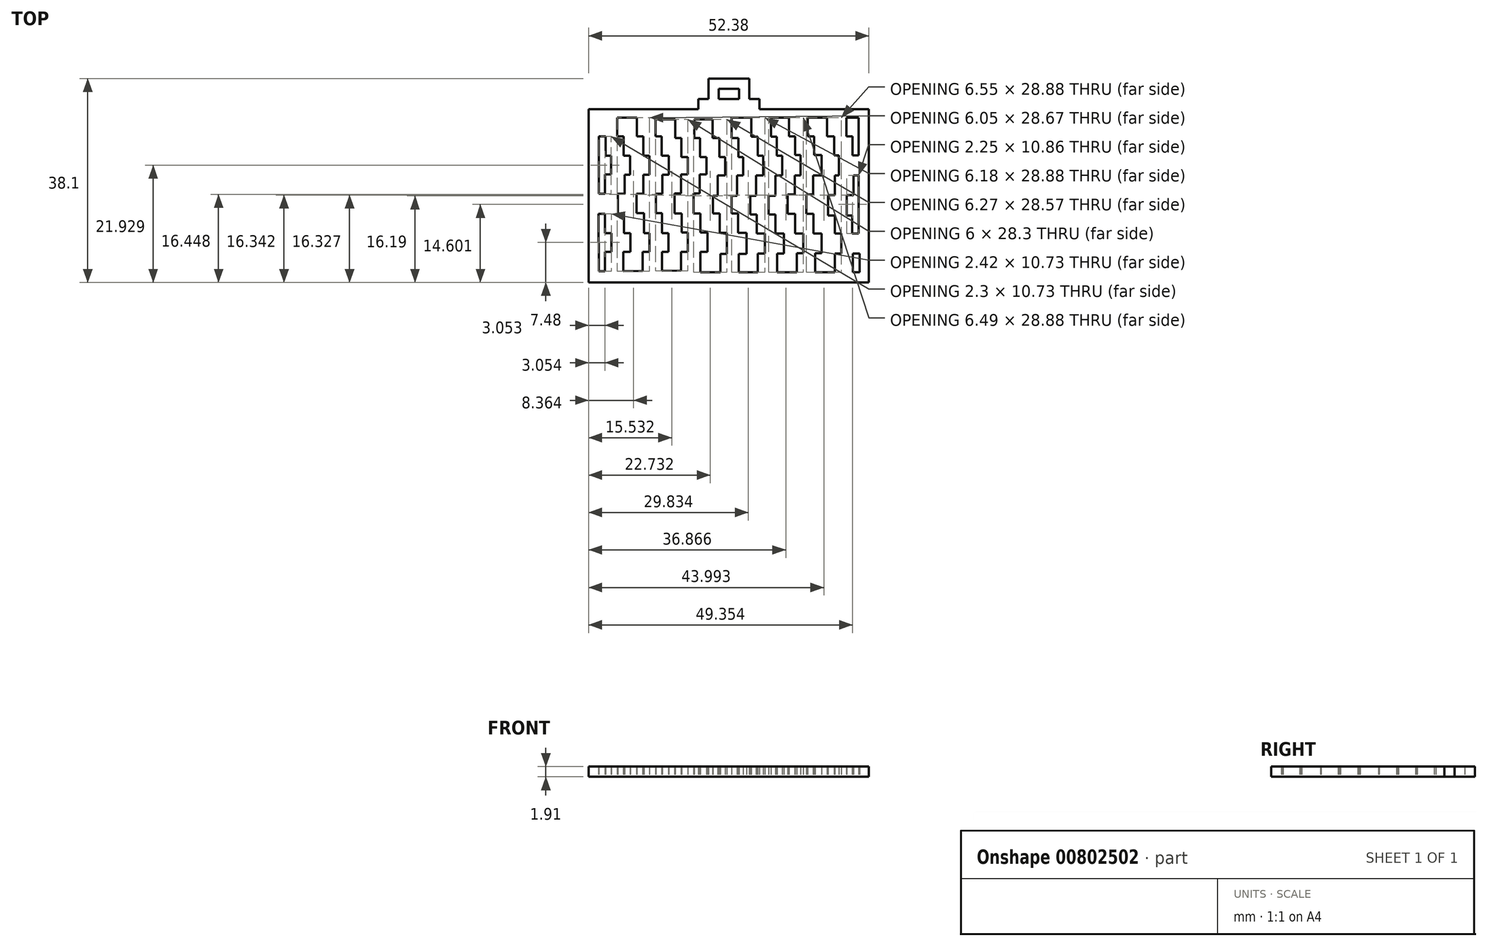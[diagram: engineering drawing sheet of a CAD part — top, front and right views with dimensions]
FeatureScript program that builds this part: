
annotation { "Feature Type Name" : "Feature", "Feature Type Description" : "" }
export const myFeature = defineFeature(function(context is Context, id is Id, definition is map)
    precondition{}
    {
        {
            var Q0;
            Q0=qCreatedBy(makeId("Top.planeOp"),FACE);
            var sketch = newSketch(context, id + "F0", { "sketchPlane" : qUnion([Q0])});
            skLineSegment(sketch, "E0.top", {"start": v(-16.2, 7.4) * mm, "end": v(-15.34, 7.4) * mm});
            skLineSegment(sketch, "E0.right", {"start": v(-13.9, 9.73) * mm, "end": v(-13.9, 7.4) * mm});
            skLineSegment(sketch, "E1.top", {"start": v(-15.34, 5) * mm, "end": v(-14.66, 5) * mm});
            skLineSegment(sketch, "E1.left", {"start": v(-15.34, 7.4) * mm, "end": v(-15.34, 5) * mm});
            skLineSegment(sketch, "E1.right", {"start": v(-13.1, 7.4) * mm, "end": v(-13.1, 5) * mm});
            skLineSegment(sketch, "E2.bottom", {"start": v(-13.1, 5) * mm, "end": v(-12.32, 5) * mm});
            skLineSegment(sketch, "E2.top", {"start": v(-12.99, 2.64) * mm, "end": v(-12.32, 2.64) * mm});
            skLineSegment(sketch, "E2.left", {"start": v(-14.66, 5) * mm, "end": v(-14.66, 2.64) * mm});
            skLineSegment(sketch, "E2.right", {"start": v(-12.32, 5) * mm, "end": v(-12.32, 2.64) * mm});
            skLineSegment(sketch, "E3.left", {"start": v(-11.46, 9.73) * mm, "end": v(-11.46, 7.4) * mm});
            skLineSegment(sketch, "E3.right", {"start": v(-9.1, 9.53) * mm, "end": v(-9.1, 7.4) * mm});
            skLineSegment(sketch, "E4.bottom", {"start": v(-9.1, 7.4) * mm, "end": v(-8.38, 7.4) * mm});
            skLineSegment(sketch, "E4.top", {"start": v(-10.65, 5.02) * mm, "end": v(-9.87, 5.02) * mm});
            skLineSegment(sketch, "E4.left", {"start": v(-10.65, 7.4) * mm, "end": v(-10.65, 5.02) * mm});
            skLineSegment(sketch, "E4.right", {"start": v(-8.38, 7.4) * mm, "end": v(-8.38, 5.02) * mm});
            skLineSegment(sketch, "E5.bottom", {"start": v(-8.38, 5.02) * mm, "end": v(-7.48, 5.02) * mm});
            skLineSegment(sketch, "E5.top", {"start": v(-8.3, 2.64) * mm, "end": v(-7.48, 2.64) * mm});
            skLineSegment(sketch, "E5.left", {"start": v(-9.87, 5.02) * mm, "end": v(-9.87, 2.64) * mm});
            skLineSegment(sketch, "E5.right", {"start": v(-7.48, 5.02) * mm, "end": v(-7.48, 2.64) * mm});
            skLineSegment(sketch, "E6.top", {"start": v(-6.66, 7.19) * mm, "end": v(-5.89, 7.19) * mm});
            skLineSegment(sketch, "E6.left", {"start": v(-6.66, 9.53) * mm, "end": v(-6.66, 7.19) * mm});
            skLineSegment(sketch, "E6.right", {"start": v(-4.3, 9.53) * mm, "end": v(-4.3, 7.19) * mm});
            skLineSegment(sketch, "E7.bottom", {"start": v(-4.3, 7.19) * mm, "end": v(-3.57, 7.19) * mm});
            skLineSegment(sketch, "E7.top", {"start": v(-5.89, 4.82) * mm, "end": v(-5.1, 4.82) * mm});
            skLineSegment(sketch, "E7.left", {"start": v(-5.89, 7.19) * mm, "end": v(-5.89, 4.82) * mm});
            skLineSegment(sketch, "E7.right", {"start": v(-3.57, 7.19) * mm, "end": v(-3.57, 4.82) * mm});
            skLineSegment(sketch, "E8.bottom", {"start": v(-3.57, 4.82) * mm, "end": v(-2.77, 4.82) * mm});
            skLineSegment(sketch, "E8.top", {"start": v(-3.63, 2.67) * mm, "end": v(-2.77, 2.67) * mm});
            skLineSegment(sketch, "E8.left", {"start": v(-5.1, 4.82) * mm, "end": v(-5.1, 2.67) * mm});
            skLineSegment(sketch, "E8.right", {"start": v(-2.77, 4.82) * mm, "end": v(-2.77, 2.67) * mm});
            skLineSegment(sketch, "E9.bottom", {"start": v(-15.44, 2.67) * mm, "end": v(-14.66, 2.67) * mm});
            skLineSegment(sketch, "E9.top", {"start": v(-13.84, 0.25) * mm, "end": v(-12.99, 0.25) * mm});
            skLineSegment(sketch, "E9.left", {"start": v(-15.44, 2.67) * mm, "end": v(-15.44, 0.25) * mm});
            skLineSegment(sketch, "E9.right", {"start": v(-12.99, 2.67) * mm, "end": v(-12.99, 0.25) * mm});
            skLineSegment(sketch, "E10.bottom", {"start": v(-15.44, 0.25) * mm, "end": v(-16.2, 0.25) * mm});
            skLineSegment(sketch, "E10.left", {"start": v(-13.84, 0.25) * mm, "end": v(-13.84, -2.23) * mm});
            skPoint(sketch, "E11.firstSnap0", {"position": v(-15.04, -2.23) * mm});
            skLineSegment(sketch, "E11.top", {"start": v(-15.44, -4.63) * mm, "end": v(-14.62, -4.63) * mm});
            skLineSegment(sketch, "E11.left", {"start": v(-15.44, -2.23) * mm, "end": v(-15.44, -4.63) * mm});
            skLineSegment(sketch, "E11.right", {"start": v(-13.04, -2.23) * mm, "end": v(-13.04, -4.63) * mm});
            skLineSegment(sketch, "E12.bottom", {"start": v(-13.04, -4.63) * mm, "end": v(-12.25, -4.63) * mm});
            skLineSegment(sketch, "E12.top", {"start": v(-13.13, -7) * mm, "end": v(-12.25, -7) * mm});
            skLineSegment(sketch, "E12.left", {"start": v(-14.62, -4.63) * mm, "end": v(-14.62, -7) * mm});
            skLineSegment(sketch, "E12.right", {"start": v(-12.25, -4.63) * mm, "end": v(-12.25, -7) * mm});
            skLineSegment(sketch, "E13.bottom", {"start": v(-14.62, -7) * mm, "end": v(-15.44, -7) * mm});
            skLineSegment(sketch, "E13.left", {"start": v(-13.13, -7) * mm, "end": v(-13.13, -9.38) * mm});
            skLineSegment(sketch, "E13.right", {"start": v(-15.44, -7) * mm, "end": v(-15.44, -9.38) * mm});
            skLineSegment(sketch, "E14.bottom", {"start": v(-9.87, 2.64) * mm, "end": v(-10.64, 2.64) * mm});
            skLineSegment(sketch, "E14.top", {"start": v(-8.3, 0.25) * mm, "end": v(-9.06, 0.25) * mm});
            skLineSegment(sketch, "E14.left", {"start": v(-8.3, 2.64) * mm, "end": v(-8.3, 0.25) * mm});
            skLineSegment(sketch, "E14.right", {"start": v(-10.64, 2.64) * mm, "end": v(-10.64, 0.25) * mm});
            skLineSegment(sketch, "E15.bottom", {"start": v(-10.64, 0.25) * mm, "end": v(-11.49, 0.25) * mm});
            skLineSegment(sketch, "E15.top", {"start": v(-10.56, -2.16) * mm, "end": v(-11.49, -2.16) * mm});
            skLineSegment(sketch, "E15.left", {"start": v(-9.06, 0.25) * mm, "end": v(-9.06, -2.16) * mm});
            skLineSegment(sketch, "E15.right", {"start": v(-11.49, 0.25) * mm, "end": v(-11.49, -2.16) * mm});
            skLineSegment(sketch, "E16.bottom", {"start": v(-9.06, -2.16) * mm, "end": v(-8.31, -2.16) * mm});
            skLineSegment(sketch, "E16.top", {"start": v(-10.56, -4.65) * mm, "end": v(-9.87, -4.65) * mm});
            skLineSegment(sketch, "E16.left", {"start": v(-10.56, -2.16) * mm, "end": v(-10.56, -4.65) * mm});
            skLineSegment(sketch, "E16.right", {"start": v(-8.31, -2.16) * mm, "end": v(-8.31, -4.65) * mm});
            skLineSegment(sketch, "E17.bottom", {"start": v(-8.31, -4.65) * mm, "end": v(-7.5, -4.65) * mm});
            skLineSegment(sketch, "E17.top", {"start": v(-8.31, -7) * mm, "end": v(-7.5, -7) * mm});
            skLineSegment(sketch, "E17.left", {"start": v(-9.87, -4.65) * mm, "end": v(-9.87, -7) * mm});
            skLineSegment(sketch, "E17.right", {"start": v(-7.5, -4.65) * mm, "end": v(-7.5, -7) * mm});
            skLineSegment(sketch, "E18.bottom", {"start": v(-10.74, -7) * mm, "end": v(-9.87, -7) * mm});
            skLineSegment(sketch, "E18.left", {"start": v(-10.74, -7) * mm, "end": v(-10.74, -9.34) * mm});
            skLineSegment(sketch, "E18.right", {"start": v(-8.31, -7) * mm, "end": v(-8.31, -9.34) * mm});
            skLineSegment(sketch, "E19.bottom", {"start": v(-5.1, 2.67) * mm, "end": v(-5.97, 2.67) * mm});
            skLineSegment(sketch, "E19.top", {"start": v(-3.63, 0.28) * mm, "end": v(-4.4, 0.28) * mm});
            skLineSegment(sketch, "E19.left", {"start": v(-3.63, 2.67) * mm, "end": v(-3.63, 0.28) * mm});
            skLineSegment(sketch, "E19.right", {"start": v(-5.97, 2.67) * mm, "end": v(-5.97, 0.28) * mm});
            skLineSegment(sketch, "E20.bottom", {"start": v(-5.97, 0.28) * mm, "end": v(-6.74, 0.28) * mm});
            skLineSegment(sketch, "E20.top", {"start": v(-5.86, -2.19) * mm, "end": v(-6.74, -2.19) * mm});
            skLineSegment(sketch, "E20.left", {"start": v(-4.4, 0.28) * mm, "end": v(-4.4, -2.19) * mm});
            skLineSegment(sketch, "E20.right", {"start": v(-6.74, 0.28) * mm, "end": v(-6.74, -2.19) * mm});
            skLineSegment(sketch, "E21.bottom", {"start": v(-4.4, -2.19) * mm, "end": v(-3.54, -2.19) * mm});
            skLineSegment(sketch, "E21.top", {"start": v(-5.86, -4.57) * mm, "end": v(-5.12, -4.57) * mm});
            skLineSegment(sketch, "E21.left", {"start": v(-5.86, -2.19) * mm, "end": v(-5.86, -4.57) * mm});
            skLineSegment(sketch, "E21.right", {"start": v(-3.54, -2.19) * mm, "end": v(-3.54, -4.57) * mm});
            skLineSegment(sketch, "E22.bottom", {"start": v(-3.54, -4.57) * mm, "end": v(-2.65, -4.57) * mm});
            skLineSegment(sketch, "E22.top", {"start": v(-3.55, -7) * mm, "end": v(-2.65, -7) * mm});
            skLineSegment(sketch, "E22.left", {"start": v(-5.12, -4.57) * mm, "end": v(-5.12, -7) * mm});
            skLineSegment(sketch, "E22.right", {"start": v(-2.65, -4.57) * mm, "end": v(-2.65, -7) * mm});
            skLineSegment(sketch, "E23.bottom", {"start": v(-5.12, -7) * mm, "end": v(-5.95, -7) * mm});
            skLineSegment(sketch, "E23.left", {"start": v(-3.55, -7) * mm, "end": v(-3.55, -9.52) * mm});
            skLineSegment(sketch, "E23.right", {"start": v(-5.95, -7) * mm, "end": v(-5.95, -9.32) * mm});
            skLineSegment(sketch, "E24.top", {"start": v(-2, 7.18) * mm, "end": v(-1.17, 7.18) * mm});
            skLineSegment(sketch, "E24.left", {"start": v(-2, 9.53) * mm, "end": v(-2, 7.18) * mm});
            skLineSegment(sketch, "E24.right", {"start": v(0.37, 9.73) * mm, "end": v(0.37, 7.18) * mm});
            skLineSegment(sketch, "E25.bottom", {"start": v(0.37, 7.18) * mm, "end": v(1.2, 7.18) * mm});
            skLineSegment(sketch, "E25.top", {"start": v(-1.17, 4.84) * mm, "end": v(-0.44, 4.84) * mm});
            skLineSegment(sketch, "E25.left", {"start": v(-1.17, 7.18) * mm, "end": v(-1.17, 4.84) * mm});
            skLineSegment(sketch, "E25.right", {"start": v(1.2, 7.18) * mm, "end": v(1.2, 4.84) * mm});
            skLineSegment(sketch, "E26.bottom", {"start": v(1.2, 4.84) * mm, "end": v(1.79, 4.84) * mm});
            skLineSegment(sketch, "E26.top", {"start": v(1.01, 2.56) * mm, "end": v(1.79, 2.56) * mm});
            skLineSegment(sketch, "E26.left", {"start": v(-0.44, 4.84) * mm, "end": v(-0.44, 2.56) * mm});
            skLineSegment(sketch, "E26.right", {"start": v(1.79, 4.84) * mm, "end": v(1.79, 2.56) * mm});
            skLineSegment(sketch, "E27.bottom", {"start": v(-0.44, 2.56) * mm, "end": v(-1.37, 2.56) * mm});
            skLineSegment(sketch, "E27.top", {"start": v(1.01, 0) * mm, "end": v(0.37, 0) * mm});
            skLineSegment(sketch, "E27.left", {"start": v(1.01, 2.56) * mm, "end": v(1.01, 0) * mm});
            skLineSegment(sketch, "E27.right", {"start": v(-1.37, 2.56) * mm, "end": v(-1.37, 0) * mm});
            skLineSegment(sketch, "E28.bottom", {"start": v(-1.37, 0) * mm, "end": v(-1.96, 0) * mm});
            skLineSegment(sketch, "E28.top", {"start": v(-1.1, -2.19) * mm, "end": v(-1.96, -2.19) * mm});
            skLineSegment(sketch, "E28.left", {"start": v(0.37, 0) * mm, "end": v(0.37, -2.19) * mm});
            skLineSegment(sketch, "E28.right", {"start": v(-1.96, 0) * mm, "end": v(-1.96, -2.19) * mm});
            skLineSegment(sketch, "E29.bottom", {"start": v(0.37, -2.19) * mm, "end": v(1.15, -2.19) * mm});
            skLineSegment(sketch, "E29.top", {"start": v(-1.1, -4.6) * mm, "end": v(-0.22, -4.6) * mm});
            skLineSegment(sketch, "E29.left", {"start": v(-1.1, -2.19) * mm, "end": v(-1.1, -4.6) * mm});
            skLineSegment(sketch, "E29.right", {"start": v(1.15, -2.19) * mm, "end": v(1.15, -4.6) * mm});
            skLineSegment(sketch, "E30.bottom", {"start": v(1.15, -4.6) * mm, "end": v(2.23, -4.6) * mm});
            skLineSegment(sketch, "E30.top", {"start": v(1.25, -7.25) * mm, "end": v(2.23, -7.25) * mm});
            skLineSegment(sketch, "E30.left", {"start": v(-0.22, -4.6) * mm, "end": v(-0.22, -7.25) * mm});
            skLineSegment(sketch, "E30.right", {"start": v(2.23, -4.6) * mm, "end": v(2.23, -7.25) * mm});
            skLineSegment(sketch, "E31.bottom", {"start": v(-0.22, -7.25) * mm, "end": v(-1.03, -7.25) * mm});
            skLineSegment(sketch, "E32.top", {"start": v(2.82, 7.38) * mm, "end": v(3.63, 7.38) * mm});
            skLineSegment(sketch, "E32.left", {"start": v(2.82, 9.73) * mm, "end": v(2.82, 7.38) * mm});
            skLineSegment(sketch, "E32.right", {"start": v(5.27, 9.73) * mm, "end": v(5.27, 7.38) * mm});
            skLineSegment(sketch, "E33.bottom", {"start": v(5.27, 7.38) * mm, "end": v(5.99, 7.38) * mm});
            skLineSegment(sketch, "E33.top", {"start": v(3.63, 5) * mm, "end": v(4.28, 5) * mm});
            skLineSegment(sketch, "E33.left", {"start": v(3.63, 7.38) * mm, "end": v(3.63, 5) * mm});
            skLineSegment(sketch, "E33.right", {"start": v(5.99, 7.38) * mm, "end": v(5.99, 5) * mm});
            skLineSegment(sketch, "E34.bottom", {"start": v(5.99, 5) * mm, "end": v(6.66, 5) * mm});
            skLineSegment(sketch, "E34.top", {"start": v(5.8, 2.56) * mm, "end": v(6.66, 2.56) * mm});
            skLineSegment(sketch, "E34.left", {"start": v(4.28, 5) * mm, "end": v(4.28, 2.56) * mm});
            skLineSegment(sketch, "E34.right", {"start": v(6.66, 5) * mm, "end": v(6.66, 2.56) * mm});
            skLineSegment(sketch, "E35.bottom", {"start": v(4.28, 2.56) * mm, "end": v(3.4, 2.56) * mm});
            skLineSegment(sketch, "E35.top", {"start": v(5.8, 0) * mm, "end": v(4.95, 0) * mm});
            skLineSegment(sketch, "E35.left", {"start": v(5.8, 2.56) * mm, "end": v(5.8, 0) * mm});
            skLineSegment(sketch, "E35.right", {"start": v(3.4, 2.56) * mm, "end": v(3.4, 0) * mm});
            skLineSegment(sketch, "E36.bottom", {"start": v(3.4, 0) * mm, "end": v(2.69, 0) * mm});
            skLineSegment(sketch, "E36.top", {"start": v(3.48, -2.33) * mm, "end": v(2.69, -2.33) * mm});
            skLineSegment(sketch, "E36.left", {"start": v(4.95, 0) * mm, "end": v(4.95, -2.33) * mm});
            skLineSegment(sketch, "E36.right", {"start": v(2.69, 0) * mm, "end": v(2.69, -2.33) * mm});
            skLineSegment(sketch, "E37.bottom", {"start": v(4.95, -2.33) * mm, "end": v(5.83, -2.33) * mm});
            skLineSegment(sketch, "E37.top", {"start": v(3.48, -4.68) * mm, "end": v(4.5, -4.68) * mm});
            skLineSegment(sketch, "E37.left", {"start": v(3.48, -2.33) * mm, "end": v(3.48, -4.68) * mm});
            skLineSegment(sketch, "E37.right", {"start": v(5.83, -2.33) * mm, "end": v(5.83, -4.68) * mm});
            skLineSegment(sketch, "E38.bottom", {"start": v(5.83, -4.68) * mm, "end": v(6.86, -4.68) * mm});
            skLineSegment(sketch, "E38.top", {"start": v(6.05, -7.17) * mm, "end": v(6.86, -7.17) * mm});
            skLineSegment(sketch, "E38.left", {"start": v(4.5, -4.68) * mm, "end": v(4.5, -7.17) * mm});
            skLineSegment(sketch, "E38.right", {"start": v(6.86, -4.68) * mm, "end": v(6.86, -7.17) * mm});
            skLineSegment(sketch, "E39.bottom", {"start": v(4.5, -7.17) * mm, "end": v(3.63, -7.17) * mm});
            skLineSegment(sketch, "E39.left", {"start": v(6.05, -7.17) * mm, "end": v(6.05, -9.52) * mm});
            skLineSegment(sketch, "E39.right", {"start": v(3.63, -7.17) * mm, "end": v(3.63, -9.52) * mm});
            skLineSegment(sketch, "E40.bottom", {"start": v(7.5, 9.73) * mm, "end": v(9.83, 9.73) * mm});
            skLineSegment(sketch, "E40.top", {"start": v(7.5, 7.4) * mm, "end": v(8.29, 7.4) * mm});
            skLineSegment(sketch, "E40.left", {"start": v(7.5, 9.73) * mm, "end": v(7.5, 7.4) * mm});
            skLineSegment(sketch, "E40.right", {"start": v(9.83, 9.73) * mm, "end": v(9.83, 7.4) * mm});
            skLineSegment(sketch, "E41.bottom", {"start": v(12.24, 9.73) * mm, "end": v(14.67, 9.73) * mm});
            skLineSegment(sketch, "E41.top", {"start": v(12.24, 7.4) * mm, "end": v(13.13, 7.4) * mm});
            skLineSegment(sketch, "E41.left", {"start": v(12.24, 9.73) * mm, "end": v(12.24, 7.4) * mm});
            skLineSegment(sketch, "E41.right", {"start": v(14.67, 9.73) * mm, "end": v(14.67, 7.4) * mm});
            skLineSegment(sketch, "E42.bottom", {"start": v(9.83, 7.4) * mm, "end": v(10.65, 7.4) * mm});
            skLineSegment(sketch, "E42.top", {"start": v(8.29, 5.07) * mm, "end": v(8.95, 5.07) * mm});
            skLineSegment(sketch, "E42.left", {"start": v(8.29, 7.4) * mm, "end": v(8.29, 5.07) * mm});
            skLineSegment(sketch, "E42.right", {"start": v(10.65, 7.4) * mm, "end": v(10.65, 5.07) * mm});
            skLineSegment(sketch, "E43.bottom", {"start": v(10.65, 5.07) * mm, "end": v(11.58, 5.07) * mm});
            skLineSegment(sketch, "E43.top", {"start": v(10.51, 2.56) * mm, "end": v(11.58, 2.56) * mm});
            skLineSegment(sketch, "E43.left", {"start": v(8.95, 5.07) * mm, "end": v(8.95, 2.56) * mm});
            skLineSegment(sketch, "E43.right", {"start": v(11.58, 5.07) * mm, "end": v(11.58, 2.56) * mm});
            skLineSegment(sketch, "E44.bottom", {"start": v(8.95, 2.56) * mm, "end": v(8.22, 2.56) * mm});
            skLineSegment(sketch, "E44.top", {"start": v(10.51, 0.18) * mm, "end": v(9.68, 0.18) * mm});
            skLineSegment(sketch, "E44.left", {"start": v(10.51, 2.56) * mm, "end": v(10.51, 0.18) * mm});
            skLineSegment(sketch, "E44.right", {"start": v(8.22, 2.56) * mm, "end": v(8.22, 0.18) * mm});
            skLineSegment(sketch, "E45.bottom", {"start": v(14.67, 7.4) * mm, "end": v(15.42, 7.4) * mm});
            skLineSegment(sketch, "E45.top", {"start": v(13.13, 5.03) * mm, "end": v(13.74, 5.03) * mm});
            skLineSegment(sketch, "E45.left", {"start": v(13.13, 7.4) * mm, "end": v(13.13, 5.03) * mm});
            skLineSegment(sketch, "E45.right", {"start": v(15.42, 7.4) * mm, "end": v(15.42, 5.03) * mm});
            skLineSegment(sketch, "E46.bottom", {"start": v(15.42, 5.03) * mm, "end": v(16.2, 5.03) * mm});
            skLineSegment(sketch, "E46.top", {"start": v(15.54, 2.56) * mm, "end": v(16.2, 2.56) * mm});
            skLineSegment(sketch, "E46.left", {"start": v(13.74, 5.03) * mm, "end": v(13.74, 2.56) * mm});
            skLineSegment(sketch, "E47.bottom", {"start": v(13.74, 2.56) * mm, "end": v(13.23, 2.56) * mm});
            skLineSegment(sketch, "E47.top", {"start": v(15.54, 0.1) * mm, "end": v(14.7, 0.1) * mm});
            skLineSegment(sketch, "E47.left", {"start": v(15.54, 2.56) * mm, "end": v(15.54, 0.1) * mm});
            skLineSegment(sketch, "E47.right", {"start": v(13.23, 2.56) * mm, "end": v(13.23, 0.1) * mm});
            skLineSegment(sketch, "E48.bottom", {"start": v(13.23, 0.1) * mm, "end": v(12.4, 0.1) * mm});
            skLineSegment(sketch, "E48.top", {"start": v(13.23, -2.47) * mm, "end": v(12.4, -2.47) * mm});
            skLineSegment(sketch, "E48.left", {"start": v(14.7, 0.1) * mm, "end": v(14.7, -2.47) * mm});
            skLineSegment(sketch, "E48.right", {"start": v(12.4, 0.1) * mm, "end": v(12.4, -2.47) * mm});
            skLineSegment(sketch, "E49.bottom", {"start": v(14.7, -2.47) * mm, "end": v(15.39, -2.47) * mm});
            skLineSegment(sketch, "E49.top", {"start": v(13.23, -4.68) * mm, "end": v(14.05, -4.68) * mm});
            skLineSegment(sketch, "E49.left", {"start": v(13.23, -2.47) * mm, "end": v(13.23, -4.68) * mm});
            skLineSegment(sketch, "E49.right", {"start": v(15.39, -2.47) * mm, "end": v(15.39, -4.68) * mm});
            skLineSegment(sketch, "E50.bottom", {"start": v(15.39, -4.68) * mm, "end": v(16.2, -4.68) * mm});
            skLineSegment(sketch, "E50.top", {"start": v(15.45, -7.2) * mm, "end": v(16.32, -7.2) * mm});
            skLineSegment(sketch, "E50.left", {"start": v(14.05, -4.68) * mm, "end": v(14.05, -7.2) * mm});
            skLineSegment(sketch, "E51.bottom", {"start": v(14.05, -7.2) * mm, "end": v(13.23, -7.2) * mm});
            skLineSegment(sketch, "E51.left", {"start": v(15.45, -7.2) * mm, "end": v(15.45, -9.52) * mm});
            skLineSegment(sketch, "E51.right", {"start": v(13.23, -7.2) * mm, "end": v(13.23, -9.52) * mm});
            skLineSegment(sketch, "E52.bottom", {"start": v(8.22, 0.18) * mm, "end": v(7.36, 0.18) * mm});
            skLineSegment(sketch, "E52.top", {"start": v(8.29, -2.24) * mm, "end": v(7.36, -2.24) * mm});
            skLineSegment(sketch, "E52.left", {"start": v(9.68, 0.18) * mm, "end": v(9.68, -2.24) * mm});
            skLineSegment(sketch, "E52.right", {"start": v(7.36, 0.18) * mm, "end": v(7.36, -2.24) * mm});
            skLineSegment(sketch, "E53.bottom", {"start": v(9.68, -2.24) * mm, "end": v(10.56, -2.24) * mm});
            skLineSegment(sketch, "E53.top", {"start": v(8.29, -4.68) * mm, "end": v(9.28, -4.68) * mm});
            skLineSegment(sketch, "E53.left", {"start": v(8.29, -2.24) * mm, "end": v(8.29, -4.68) * mm});
            skLineSegment(sketch, "E53.right", {"start": v(10.56, -2.24) * mm, "end": v(10.56, -4.68) * mm});
            skLineSegment(sketch, "E54.bottom", {"start": v(10.56, -4.68) * mm, "end": v(11.58, -4.68) * mm});
            skLineSegment(sketch, "E54.top", {"start": v(10.77, -7.15) * mm, "end": v(11.58, -7.15) * mm});
            skLineSegment(sketch, "E54.left", {"start": v(9.28, -4.68) * mm, "end": v(9.28, -7.15) * mm});
            skLineSegment(sketch, "E54.right", {"start": v(11.58, -4.68) * mm, "end": v(11.58, -7.15) * mm});
            skLineSegment(sketch, "E55.bottom", {"start": v(9.28, -7.15) * mm, "end": v(8.47, -7.15) * mm});
            skLineSegment(sketch, "E55.left", {"start": v(10.77, -7.15) * mm, "end": v(10.77, -9.52) * mm});
            skLineSegment(sketch, "E56", {"start": v(-13.9, 7.4) * mm, "end": v(-13.1, 7.4) * mm});
            skLineSegment(sketch, "E57.trimOffspring", {"start": v(-13.84, -2.23) * mm, "end": v(-13.04, -2.23) * mm});
            skLineSegment(sketch, "E58", {"start": v(-16.23, -2.23) * mm, "end": v(-15.44, -2.23) * mm});
            skLineSegment(sketch, "E59", {"start": v(-13.9, 9.73) * mm, "end": v(-11.46, 9.73) * mm});
            skLineSegment(sketch, "E60", {"start": v(-9.1, 9.53) * mm, "end": v(-6.66, 9.53) * mm});
            skLineSegment(sketch, "E61", {"start": v(-4.3, 9.53) * mm, "end": v(-2, 9.53) * mm});
            skLineSegment(sketch, "E62", {"start": v(2.82, 9.73) * mm, "end": v(0.37, 9.73) * mm});
            skLineSegment(sketch, "E63", {"start": v(5.27, 9.73) * mm, "end": v(7.5, 9.73) * mm});
            skLineSegment(sketch, "E64", {"start": v(9.83, 9.73) * mm, "end": v(12.24, 9.73) * mm});
            skPoint(sketch, "E65.firstSnap0", {"position": v(-0.88, 13.65) * mm});
            skLineSegment(sketch, "E66", {"start": v(-11.46, 7.4) * mm, "end": v(-10.65, 7.4) * mm});
            skPoint(sketch, "E67.end.orphan", {"position": v(14.56, 13.65) * mm});
            skPoint(sketch, "E68.end.orphan", {"position": v(-16.3, 13.65) * mm});
            skPoint(sketch, "E65.left.start.orphan", {"position": v(-0.88, 12.48) * mm});
            skLineSegment(sketch, "E69", {"start": v(-16.2, 7.4) * mm, "end": v(-16.2, 0.25) * mm});
            skLineSegment(sketch, "E70", {"start": v(-16.23, -2.23) * mm, "end": v(-16.2, -9.38) * mm});
            skLineSegment(sketch, "E71", {"start": v(-16.2, -9.38) * mm, "end": v(-15.44, -9.38) * mm});
            skLineSegment(sketch, "E72", {"start": v(-13.13, -9.38) * mm, "end": v(-10.74, -9.34) * mm});
            skLineSegment(sketch, "E73", {"start": v(-8.31, -9.34) * mm, "end": v(-5.95, -9.32) * mm});
            skLineSegment(sketch, "E74", {"start": v(-1.03, -7.25) * mm, "end": v(-1.03, -9.52) * mm});
            skLineSegment(sketch, "E75", {"start": v(-1.03, -9.52) * mm, "end": v(-3.55, -9.52) * mm});
            skLineSegment(sketch, "E76", {"start": v(1.25, -9.52) * mm, "end": v(3.63, -9.52) * mm});
            skLineSegment(sketch, "E77", {"start": v(1.25, -7.25) * mm, "end": v(1.25, -9.52) * mm});
            skLineSegment(sketch, "E78", {"start": v(12.54, -9.52) * mm, "end": v(13.23, -9.52) * mm});
            skLineSegment(sketch, "E79", {"start": v(16.2, 5.03) * mm, "end": v(16.2, 9.73) * mm});
            skLineSegment(sketch, "E80", {"start": v(14.67, 9.73) * mm, "end": v(16.2, 9.73) * mm});
            skLineSegment(sketch, "E81", {"start": v(8.47, -7.15) * mm, "end": v(8.47, -9.52) * mm});
            skLineSegment(sketch, "E82.bottom", {"start": v(-17.46, 10.8) * mm, "end": v(-3.81, 10.8) * mm});
            skLineSegment(sketch, "E82.top", {"start": v(-17.46, -10.8) * mm, "end": v(17.46, -10.8) * mm});
            skLineSegment(sketch, "E82.left", {"start": v(-17.46, 10.8) * mm, "end": v(-17.46, -10.8) * mm});
            skLineSegment(sketch, "E82.right", {"start": v(17.46, 10.8) * mm, "end": v(17.46, -10.8) * mm});
            skLineSegment(sketch, "E83.trimOffspring", {"start": v(6.05, -9.52) * mm, "end": v(8.47, -9.52) * mm});
            skLineSegment(sketch, "E84.trimOffspring", {"start": v(10.77, -9.52) * mm, "end": v(12.54, -9.52) * mm});
            skLineSegment(sketch, "E85.trimOffspring", {"start": v(15.45, -9.52) * mm, "end": v(16.32, -9.52) * mm});
            skLineSegment(sketch, "E86.trimOffspring", {"start": v(16.32, -7.2) * mm, "end": v(16.32, -9.52) * mm});
            skLineSegment(sketch, "E87", {"start": v(16.2, 2.56) * mm, "end": v(16.2, -4.68) * mm});
            skLineSegment(sketch, "E88.bottom", {"start": v(1.27, 13.34) * mm, "end": v(-1.27, 13.34) * mm});
            skLineSegment(sketch, "E88.top", {"start": v(1.27, 12.07) * mm, "end": v(-1.27, 12.07) * mm});
            skLineSegment(sketch, "E88.left", {"start": v(1.27, 13.34) * mm, "end": v(1.27, 12.07) * mm});
            skLineSegment(sketch, "E88.right", {"start": v(-1.27, 13.34) * mm, "end": v(-1.27, 12.07) * mm});
            skLineSegment(sketch, "E89", {"start": v(-3.81, 10.8) * mm, "end": v(-3.81, 12.07) * mm});
            skLineSegment(sketch, "E90", {"start": v(-3.81, 12.07) * mm, "end": v(-2.54, 12.07) * mm});
            skLineSegment(sketch, "E91", {"start": v(-2.54, 12.07) * mm, "end": v(-2.54, 14.6) * mm});
            skLineSegment(sketch, "E92", {"start": v(-2.54, 14.6) * mm, "end": v(2.54, 14.6) * mm});
            skLineSegment(sketch, "E93", {"start": v(2.54, 14.6) * mm, "end": v(2.54, 12.07) * mm});
            skLineSegment(sketch, "E94", {"start": v(2.54, 12.07) * mm, "end": v(3.81, 12.07) * mm});
            skLineSegment(sketch, "E95", {"start": v(3.81, 12.07) * mm, "end": v(3.81, 10.8) * mm});
            skLineSegment(sketch, "E96.trimOffspring", {"start": v(3.81, 10.8) * mm, "end": v(17.46, 10.8) * mm});
            skSolve(sketch);
        }
        {
            var Q0;
            Q0 = qSketchRegion(id + "F0", true);
            extrude(context, id + "F1", {"entities" : qUnion([Q0]), "depth" : 1.27 * mm, "offsetDistance" : 25.4 * mm});
        }
        {
            var Q0;
            Q0=makeQuery(id+"F1.opExtrude","SWEPT_BODY",BODY,{"disambiguationData":[OSD([sQuery(id+"F0.wireOp",EDGE,"E0.top"),sQuery(id+"F0.wireOp",EDGE,"E0.right"),sQuery(id+"F0.wireOp",EDGE,"E1.top"),sQuery(id+"F0.wireOp",EDGE,"E1.left"),sQuery(id+"F0.wireOp",EDGE,"E1.right"),sQuery(id+"F0.wireOp",EDGE,"E2.bottom"),sQuery(id+"F0.wireOp",EDGE,"E2.top"),sQuery(id+"F0.wireOp",EDGE,"E2.left"),sQuery(id+"F0.wireOp",EDGE,"E2.right"),sQuery(id+"F0.wireOp",EDGE,"E3.left"),sQuery(id+"F0.wireOp",EDGE,"E3.right"),sQuery(id+"F0.wireOp",EDGE,"E4.bottom"),sQuery(id+"F0.wireOp",EDGE,"E4.top"),sQuery(id+"F0.wireOp",EDGE,"E4.left"),sQuery(id+"F0.wireOp",EDGE,"E4.right"),sQuery(id+"F0.wireOp",EDGE,"E5.bottom"),sQuery(id+"F0.wireOp",EDGE,"E5.top"),sQuery(id+"F0.wireOp",EDGE,"E5.left"),sQuery(id+"F0.wireOp",EDGE,"E5.right"),sQuery(id+"F0.wireOp",EDGE,"E6.top"),sQuery(id+"F0.wireOp",EDGE,"E6.left"),sQuery(id+"F0.wireOp",EDGE,"E6.right"),sQuery(id+"F0.wireOp",EDGE,"E7.bottom"),sQuery(id+"F0.wireOp",EDGE,"E7.top"),sQuery(id+"F0.wireOp",EDGE,"E7.left"),sQuery(id+"F0.wireOp",EDGE,"E7.right"),sQuery(id+"F0.wireOp",EDGE,"E8.bottom"),sQuery(id+"F0.wireOp",EDGE,"E8.top"),sQuery(id+"F0.wireOp",EDGE,"E8.left"),sQuery(id+"F0.wireOp",EDGE,"E8.right"),sQuery(id+"F0.wireOp",EDGE,"E9.bottom"),sQuery(id+"F0.wireOp",EDGE,"E9.top"),sQuery(id+"F0.wireOp",EDGE,"E9.left"),sQuery(id+"F0.wireOp",EDGE,"E9.right"),sQuery(id+"F0.wireOp",EDGE,"E10.bottom"),sQuery(id+"F0.wireOp",EDGE,"E10.left"),sQuery(id+"F0.wireOp",EDGE,"E11.top"),sQuery(id+"F0.wireOp",EDGE,"E11.left"),sQuery(id+"F0.wireOp",EDGE,"E11.right"),sQuery(id+"F0.wireOp",EDGE,"E12.bottom"),sQuery(id+"F0.wireOp",EDGE,"E12.top"),sQuery(id+"F0.wireOp",EDGE,"E12.left"),sQuery(id+"F0.wireOp",EDGE,"E12.right"),sQuery(id+"F0.wireOp",EDGE,"E13.bottom"),sQuery(id+"F0.wireOp",EDGE,"E13.left"),sQuery(id+"F0.wireOp",EDGE,"E13.right"),sQuery(id+"F0.wireOp",EDGE,"E14.bottom"),sQuery(id+"F0.wireOp",EDGE,"E14.top"),sQuery(id+"F0.wireOp",EDGE,"E14.left"),sQuery(id+"F0.wireOp",EDGE,"E14.right"),sQuery(id+"F0.wireOp",EDGE,"E15.bottom"),sQuery(id+"F0.wireOp",EDGE,"E15.top"),sQuery(id+"F0.wireOp",EDGE,"E15.left"),sQuery(id+"F0.wireOp",EDGE,"E15.right"),sQuery(id+"F0.wireOp",EDGE,"E16.bottom"),sQuery(id+"F0.wireOp",EDGE,"E16.top"),sQuery(id+"F0.wireOp",EDGE,"E16.left"),sQuery(id+"F0.wireOp",EDGE,"E16.right"),sQuery(id+"F0.wireOp",EDGE,"E17.bottom"),sQuery(id+"F0.wireOp",EDGE,"E17.top"),sQuery(id+"F0.wireOp",EDGE,"E17.left"),sQuery(id+"F0.wireOp",EDGE,"E17.right"),sQuery(id+"F0.wireOp",EDGE,"E18.bottom"),sQuery(id+"F0.wireOp",EDGE,"E18.left"),sQuery(id+"F0.wireOp",EDGE,"E18.right"),sQuery(id+"F0.wireOp",EDGE,"E19.bottom"),sQuery(id+"F0.wireOp",EDGE,"E19.top"),sQuery(id+"F0.wireOp",EDGE,"E19.left"),sQuery(id+"F0.wireOp",EDGE,"E19.right"),sQuery(id+"F0.wireOp",EDGE,"E20.bottom"),sQuery(id+"F0.wireOp",EDGE,"E20.top"),sQuery(id+"F0.wireOp",EDGE,"E20.left"),sQuery(id+"F0.wireOp",EDGE,"E20.right"),sQuery(id+"F0.wireOp",EDGE,"E21.bottom"),sQuery(id+"F0.wireOp",EDGE,"E21.top"),sQuery(id+"F0.wireOp",EDGE,"E21.left"),sQuery(id+"F0.wireOp",EDGE,"E21.right"),sQuery(id+"F0.wireOp",EDGE,"E22.bottom"),sQuery(id+"F0.wireOp",EDGE,"E22.top"),sQuery(id+"F0.wireOp",EDGE,"E22.left"),sQuery(id+"F0.wireOp",EDGE,"E22.right"),sQuery(id+"F0.wireOp",EDGE,"E23.bottom"),sQuery(id+"F0.wireOp",EDGE,"E23.left"),sQuery(id+"F0.wireOp",EDGE,"E23.right"),sQuery(id+"F0.wireOp",EDGE,"E24.top"),sQuery(id+"F0.wireOp",EDGE,"E24.left"),sQuery(id+"F0.wireOp",EDGE,"E24.right"),sQuery(id+"F0.wireOp",EDGE,"E25.bottom"),sQuery(id+"F0.wireOp",EDGE,"E25.top"),sQuery(id+"F0.wireOp",EDGE,"E25.left"),sQuery(id+"F0.wireOp",EDGE,"E25.right"),sQuery(id+"F0.wireOp",EDGE,"E26.bottom"),sQuery(id+"F0.wireOp",EDGE,"E26.top"),sQuery(id+"F0.wireOp",EDGE,"E26.left"),sQuery(id+"F0.wireOp",EDGE,"E26.right"),sQuery(id+"F0.wireOp",EDGE,"E27.bottom"),sQuery(id+"F0.wireOp",EDGE,"E27.top"),sQuery(id+"F0.wireOp",EDGE,"E27.left"),sQuery(id+"F0.wireOp",EDGE,"E27.right"),sQuery(id+"F0.wireOp",EDGE,"E28.top"),sQuery(id+"F0.wireOp",EDGE,"E28.left"),sQuery(id+"F0.wireOp",EDGE,"E28.right"),sQuery(id+"F0.wireOp",EDGE,"E29.bottom"),sQuery(id+"F0.wireOp",EDGE,"E29.top"),sQuery(id+"F0.wireOp",EDGE,"E29.left"),sQuery(id+"F0.wireOp",EDGE,"E29.right"),sQuery(id+"F0.wireOp",EDGE,"E30.bottom"),sQuery(id+"F0.wireOp",EDGE,"E30.top"),sQuery(id+"F0.wireOp",EDGE,"E30.left"),sQuery(id+"F0.wireOp",EDGE,"E30.right"),sQuery(id+"F0.wireOp",EDGE,"E31.bottom"),sQuery(id+"F0.wireOp",EDGE,"E32.top"),sQuery(id+"F0.wireOp",EDGE,"E32.left"),sQuery(id+"F0.wireOp",EDGE,"E32.right"),sQuery(id+"F0.wireOp",EDGE,"E33.bottom"),sQuery(id+"F0.wireOp",EDGE,"E33.top"),sQuery(id+"F0.wireOp",EDGE,"E33.left"),sQuery(id+"F0.wireOp",EDGE,"E33.right"),sQuery(id+"F0.wireOp",EDGE,"E34.bottom"),sQuery(id+"F0.wireOp",EDGE,"E34.top"),sQuery(id+"F0.wireOp",EDGE,"E34.left"),sQuery(id+"F0.wireOp",EDGE,"E34.right"),sQuery(id+"F0.wireOp",EDGE,"E35.bottom"),sQuery(id+"F0.wireOp",EDGE,"E35.top"),sQuery(id+"F0.wireOp",EDGE,"E35.left"),sQuery(id+"F0.wireOp",EDGE,"E35.right"),sQuery(id+"F0.wireOp",EDGE,"E36.bottom"),sQuery(id+"F0.wireOp",EDGE,"E36.top"),sQuery(id+"F0.wireOp",EDGE,"E36.left"),sQuery(id+"F0.wireOp",EDGE,"E36.right"),sQuery(id+"F0.wireOp",EDGE,"E37.bottom"),sQuery(id+"F0.wireOp",EDGE,"E37.top"),sQuery(id+"F0.wireOp",EDGE,"E37.left"),sQuery(id+"F0.wireOp",EDGE,"E37.right"),sQuery(id+"F0.wireOp",EDGE,"E38.bottom"),sQuery(id+"F0.wireOp",EDGE,"E38.top"),sQuery(id+"F0.wireOp",EDGE,"E38.left"),sQuery(id+"F0.wireOp",EDGE,"E38.right"),sQuery(id+"F0.wireOp",EDGE,"E39.bottom"),sQuery(id+"F0.wireOp",EDGE,"E39.left"),sQuery(id+"F0.wireOp",EDGE,"E39.right"),sQuery(id+"F0.wireOp",EDGE,"E40.top"),sQuery(id+"F0.wireOp",EDGE,"E40.left"),sQuery(id+"F0.wireOp",EDGE,"E40.right"),sQuery(id+"F0.wireOp",EDGE,"E41.top"),sQuery(id+"F0.wireOp",EDGE,"E41.left"),sQuery(id+"F0.wireOp",EDGE,"E41.right"),sQuery(id+"F0.wireOp",EDGE,"E42.bottom"),sQuery(id+"F0.wireOp",EDGE,"E42.top"),sQuery(id+"F0.wireOp",EDGE,"E42.left"),sQuery(id+"F0.wireOp",EDGE,"E42.right"),sQuery(id+"F0.wireOp",EDGE,"E43.bottom"),sQuery(id+"F0.wireOp",EDGE,"E43.top"),sQuery(id+"F0.wireOp",EDGE,"E43.left"),sQuery(id+"F0.wireOp",EDGE,"E43.right"),sQuery(id+"F0.wireOp",EDGE,"E44.bottom"),sQuery(id+"F0.wireOp",EDGE,"E44.top"),sQuery(id+"F0.wireOp",EDGE,"E44.left"),sQuery(id+"F0.wireOp",EDGE,"E44.right"),sQuery(id+"F0.wireOp",EDGE,"E45.bottom"),sQuery(id+"F0.wireOp",EDGE,"E45.top"),sQuery(id+"F0.wireOp",EDGE,"E45.left"),sQuery(id+"F0.wireOp",EDGE,"E45.right"),sQuery(id+"F0.wireOp",EDGE,"E46.bottom"),sQuery(id+"F0.wireOp",EDGE,"E46.top"),sQuery(id+"F0.wireOp",EDGE,"E46.left"),sQuery(id+"F0.wireOp",EDGE,"E47.bottom"),sQuery(id+"F0.wireOp",EDGE,"E47.top"),sQuery(id+"F0.wireOp",EDGE,"E47.left"),sQuery(id+"F0.wireOp",EDGE,"E47.right"),sQuery(id+"F0.wireOp",EDGE,"E48.bottom"),sQuery(id+"F0.wireOp",EDGE,"E48.top"),sQuery(id+"F0.wireOp",EDGE,"E48.left"),sQuery(id+"F0.wireOp",EDGE,"E48.right"),sQuery(id+"F0.wireOp",EDGE,"E49.bottom"),sQuery(id+"F0.wireOp",EDGE,"E49.top"),sQuery(id+"F0.wireOp",EDGE,"E49.left"),sQuery(id+"F0.wireOp",EDGE,"E49.right"),sQuery(id+"F0.wireOp",EDGE,"E50.bottom"),sQuery(id+"F0.wireOp",EDGE,"E50.top"),sQuery(id+"F0.wireOp",EDGE,"E50.left"),sQuery(id+"F0.wireOp",EDGE,"E51.bottom"),sQuery(id+"F0.wireOp",EDGE,"E51.left"),sQuery(id+"F0.wireOp",EDGE,"E51.right"),sQuery(id+"F0.wireOp",EDGE,"E52.bottom"),sQuery(id+"F0.wireOp",EDGE,"E52.top"),sQuery(id+"F0.wireOp",EDGE,"E52.left"),sQuery(id+"F0.wireOp",EDGE,"E52.right"),sQuery(id+"F0.wireOp",EDGE,"E53.bottom"),sQuery(id+"F0.wireOp",EDGE,"E53.top"),sQuery(id+"F0.wireOp",EDGE,"E53.left"),sQuery(id+"F0.wireOp",EDGE,"E53.right"),sQuery(id+"F0.wireOp",EDGE,"E54.bottom"),sQuery(id+"F0.wireOp",EDGE,"E54.top"),sQuery(id+"F0.wireOp",EDGE,"E54.left"),sQuery(id+"F0.wireOp",EDGE,"E54.right"),sQuery(id+"F0.wireOp",EDGE,"E55.bottom"),sQuery(id+"F0.wireOp",EDGE,"E55.left"),sQuery(id+"F0.wireOp",EDGE,"E56"),sQuery(id+"F0.wireOp",EDGE,"E57.trimOffspring"),sQuery(id+"F0.wireOp",EDGE,"E58"),sQuery(id+"F0.wireOp",EDGE,"E28.bottom"),sQuery(id+"F0.wireOp",EDGE,"E59"),sQuery(id+"F0.wireOp",EDGE,"E60"),sQuery(id+"F0.wireOp",EDGE,"E61"),sQuery(id+"F0.wireOp",EDGE,"E62"),sQuery(id+"F0.wireOp",EDGE,"E63"),sQuery(id+"F0.wireOp",EDGE,"E64"),sQuery(id+"F0.wireOp",EDGE,"E66"),sQuery(id+"F0.wireOp",EDGE,"E69"),sQuery(id+"F0.wireOp",EDGE,"E70"),sQuery(id+"F0.wireOp",EDGE,"E71"),sQuery(id+"F0.wireOp",EDGE,"E72"),sQuery(id+"F0.wireOp",EDGE,"E73"),sQuery(id+"F0.wireOp",EDGE,"E74"),sQuery(id+"F0.wireOp",EDGE,"E75"),sQuery(id+"F0.wireOp",EDGE,"E76"),sQuery(id+"F0.wireOp",EDGE,"E77"),sQuery(id+"F0.wireOp",EDGE,"E78"),sQuery(id+"F0.wireOp",EDGE,"E79"),sQuery(id+"F0.wireOp",EDGE,"E80"),sQuery(id+"F0.wireOp",EDGE,"E81"),sQuery(id+"F0.wireOp",EDGE,"E82.bottom"),sQuery(id+"F0.wireOp",EDGE,"E82.top"),sQuery(id+"F0.wireOp",EDGE,"E82.left"),sQuery(id+"F0.wireOp",EDGE,"E82.right"),sQuery(id+"F0.wireOp",EDGE,"E83.trimOffspring"),sQuery(id+"F0.wireOp",EDGE,"E84.trimOffspring"),sQuery(id+"F0.wireOp",EDGE,"E85.trimOffspring"),sQuery(id+"F0.wireOp",EDGE,"E86.trimOffspring"),sQuery(id+"F0.wireOp",EDGE,"E87"),sQuery(id+"F0.wireOp",EDGE,"E88.bottom"),sQuery(id+"F0.wireOp",EDGE,"E88.top"),sQuery(id+"F0.wireOp",EDGE,"E88.left"),sQuery(id+"F0.wireOp",EDGE,"E88.right"),sQuery(id+"F0.wireOp",EDGE,"E89"),sQuery(id+"F0.wireOp",EDGE,"E90"),sQuery(id+"F0.wireOp",EDGE,"E91"),sQuery(id+"F0.wireOp",EDGE,"E92"),sQuery(id+"F0.wireOp",EDGE,"E93"),sQuery(id+"F0.wireOp",EDGE,"E94"),sQuery(id+"F0.wireOp",EDGE,"E95"),sQuery(id+"F0.wireOp",EDGE,"E96.trimOffspring")])]});
            var Q1;
            Q1=qCreatedBy(makeId("Origin.pointOp"),VERTEX);
            transform(context, id + "F2", {"entities" : qUnion([Q0]), "transformType" : TransformType.SCALE_UNIFORMLY, "scale" : 1.5, "scalePoint" : qUnion([Q1]), "makeCopy" : false});
        }
    });
